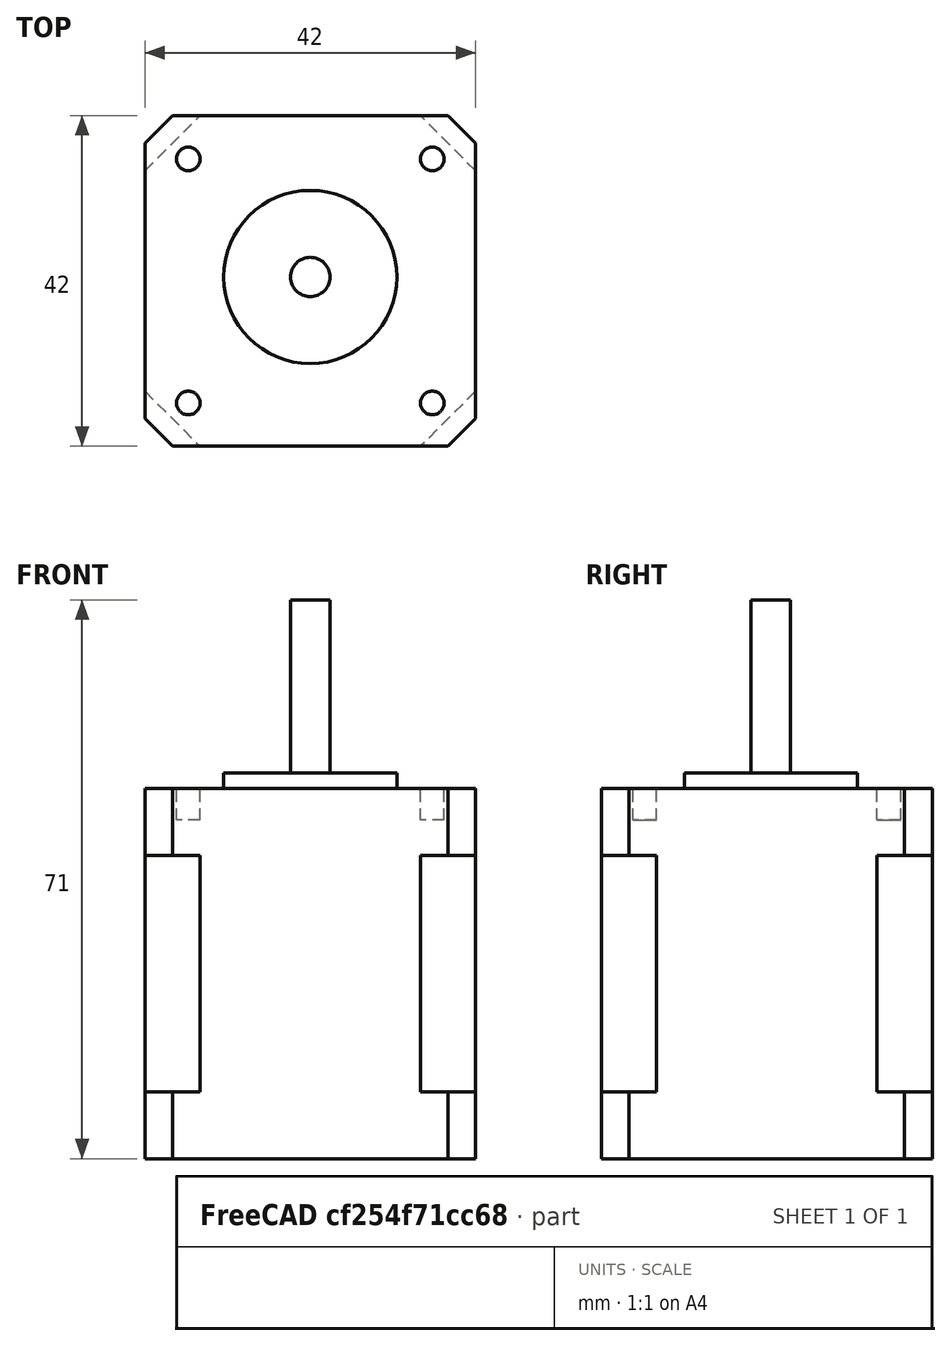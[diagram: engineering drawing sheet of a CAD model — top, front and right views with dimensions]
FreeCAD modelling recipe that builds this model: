
FCSTD DOCUMENT  (FreeCAD 0.14R3700 (Git))
Label: Nema17
License: CC-BY 3.0
LicenseURL: http://creativecommons.org/licenses/by/3.0/
objects: Part::Cylinder×6, Part::Cut×4, Part::Chamfer×3, Part::MultiFuse×3, App::MeasureDistance×3
note: 16 computed .brp shape members not serialized (recipe doc carries the construction recipe); baked Part::Feature solids carry a one-line shape summary decoded from their .brp

FEATURE [Part::Chamfer] Chamfer
  Edges = 4 edges r=7: [Edge2,Edge4,Edge6,Edge8]
FEATURE [Part::Chamfer] Chamfer001
  Edges = 4 edges r=3.5: [Edge2,Edge4,Edge6,Edge8]
FEATURE [Part::Chamfer] Chamfer002
  Edges = 4 edges r=3.5: [Edge2,Edge4,Edge6,Edge8]
FEATURE [Part::MultiFuse] Fusion
  Placement = pos=(0,0,0) rot=(1,0,0;1.5708rad)
  Shapes = -> [Chamfer002,Chamfer001,Chamfer]
FEATURE [Part::Cylinder] Cylinder
  Angle = 360
  Height = 2
  Placement = pos=(28,-23,52) rot=(0,0,1;0rad)
  Radius = 11
FEATURE [Part::Cylinder] Cylinder001
  Angle = 360
  Height = 22
  Placement = pos=(28,-23,54) rot=(0,0,1;0rad)
  Radius = 2.5
FEATURE [Part::Cylinder] Cylinder002  label="M3-1"
  Angle = 360
  Height = 5
  Placement = pos=(12.5,-8,48) rot=(0,0,1;0rad)
  Radius = 1.5
FEATURE [Part::Cylinder] Cylinder003  label="M3-002"
  Angle = 360
  Height = 5
  Placement = pos=(43.5,-8,48) rot=(0,0,1;0rad)
  Radius = 1.5
FEATURE [Part::Cylinder] Cylinder004  label="M3-003"
  Angle = 360
  Height = 5
  Placement = pos=(12.5,-39,48) rot=(0,0,1;0rad)
  Radius = 1.5
FEATURE [Part::Cylinder] Cylinder005  label="M3-004"
  Angle = 360
  Height = 5
  Placement = pos=(43.5,-39,48) rot=(0,0,1;0rad)
  Radius = 1.5
FEATURE [App::MeasureDistance] Distance  label="Distance: 30.000"
  Distance = 28
  P1 = (12.5,-9.5,53)
  P2 = (12.5,-37.5,53)
FEATURE [App::MeasureDistance] Distance001  label="Distance: 30.001"
  Distance = 28
  P1 = (14,-8,53)
  P2 = (42,-8,53)
FEATURE [App::MeasureDistance] Distance002  label="Distance: 4.000"
  Distance = 4
  P1 = (12.5,-40.5,52)
  P2 = (12.5,-44.5,52)
FEATURE [Part::Cut] Cut
  Base = -> Fusion
  Tool = -> Cylinder004
FEATURE [Part::Cut] Cut001
  Base = -> Cut
  Tool = -> Cylinder005
FEATURE [Part::Cut] Cut002
  Base = -> Cut001
  Tool = -> Cylinder002
FEATURE [Part::Cut] Cut003
  Base = -> Cut002
  Tool = -> Cylinder003
FEATURE [Part::MultiFuse] Fusion001
  Shapes = -> [Cylinder,Cylinder001]
FEATURE [Part::MultiFuse] Fusion002  label="Nema17"
  Shapes = -> [Cut003,Fusion001]
